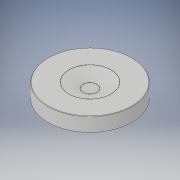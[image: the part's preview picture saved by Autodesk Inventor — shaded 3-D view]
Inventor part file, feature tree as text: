
AUTODESK INVENTOR PART (.ipt)
format: ipt  version: 2019.4 (Build 234330000, 330)  size: 125,952 bytes
history: native  units: mm
features: fillet x3, other x1, revolve x1, sketch x1
ambient origin geometry x8: Origin, YZ Plane, XZ Plane, XY Plane, X Axis, Y Axis, Z Axis, Center Point
bodies: Body1 (feature_tree)
feature tree (6):
  other  "Sólido1"
  revolve  "Revolución1"  [1 undecoded]
  fillet  "Empalme1"  Radius=1000.0mm
  fillet  "Empalme2"  Radius=500.0mm
  fillet  "Empalme3"  Radius=500.0mm
  sketch  "Boceto1"  dims[d0=1000.0mm d1=3000.0mm d2=1000.0mm d4=500.0mm d5=500.0mm d6=90.0deg d7=30.0mm d8=30.0mm d9=30.0mm]
note: 1 required parameter value undecoded (feature->parameter linkage not recoverable at this tier; creation-order binding heuristic only, values carry confidence <= 0.55)
